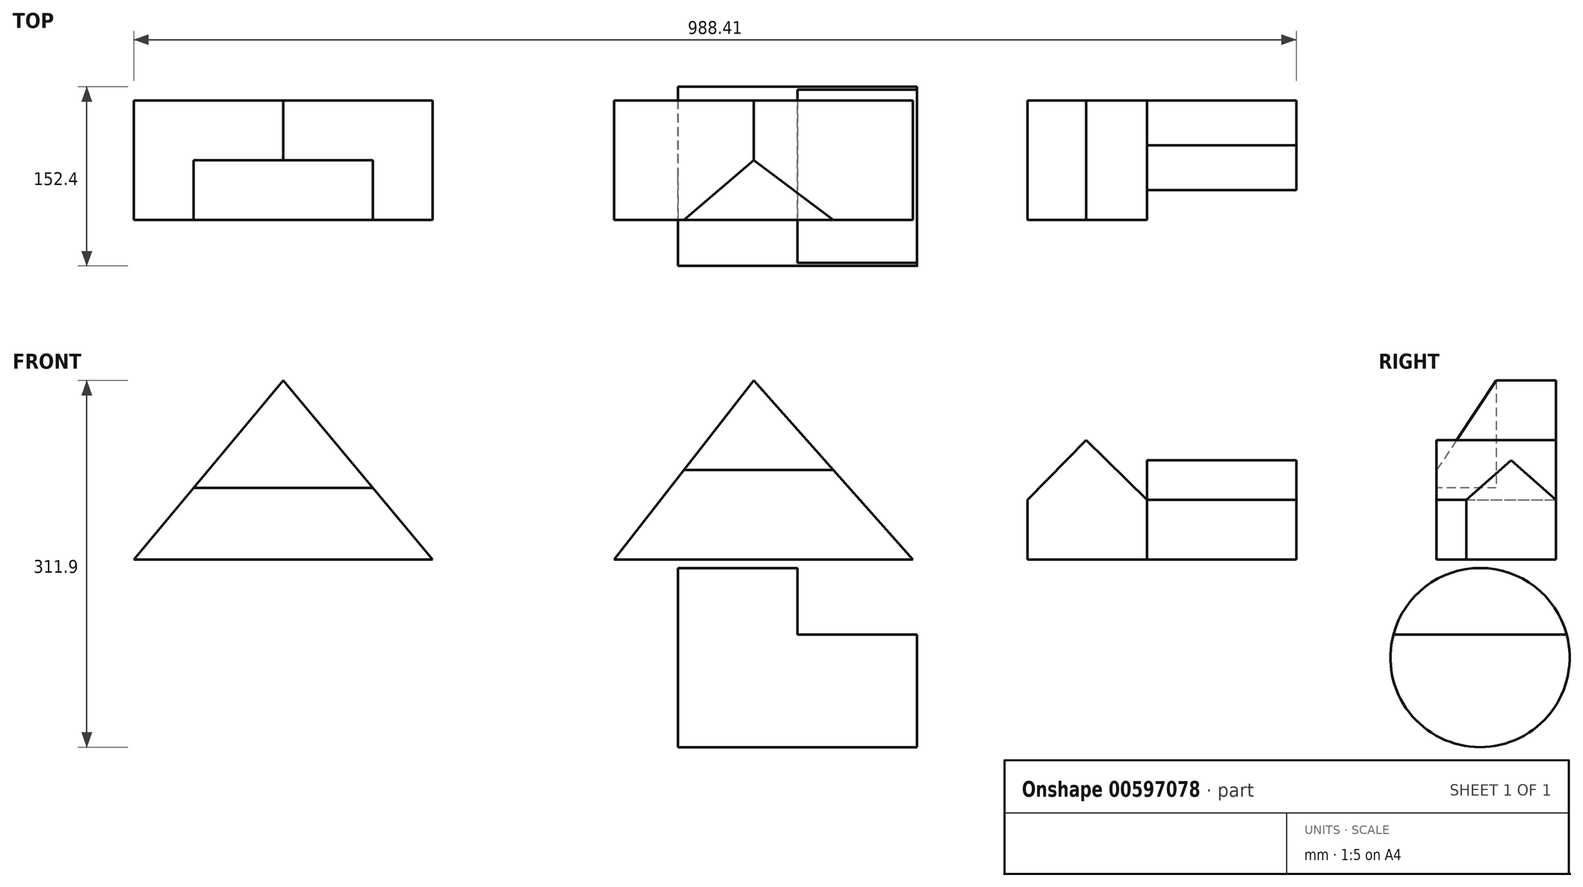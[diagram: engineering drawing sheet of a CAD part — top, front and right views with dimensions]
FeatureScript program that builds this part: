
annotation { "Feature Type Name" : "Feature", "Feature Type Description" : "" }
export const myFeature = defineFeature(function(context is Context, id is Id, definition is map)
    precondition{}
    {
        {
            var Q0;
            Q0=qCreatedBy(makeId("Front.planeOp"),FACE);
            var sketch = newSketch(context, id + "F0", { "sketchPlane" : qUnion([Q0])});
            skLineSegment(sketch, "E0", {"start": v(-127, 0) * mm, "end": v(127, 0) * mm});
            skLineSegment(sketch, "E1", {"start": v(127, 0) * mm, "end": v(0, 152.4) * mm});
            skLineSegment(sketch, "E2", {"start": v(0, 152.4) * mm, "end": v(-127, 0) * mm});
            skSolve(sketch);
        }
        {
            var Q0;
            Q0 = qSketchRegion(id + "F0", true);
            extrude(context, id + "F1", {"entities" : qUnion([Q0]), "depth" : 101.6 * mm, "offsetDistance" : 25.4 * mm});
        }
        {
            var Q0;
            Q0=makeQuery(id+"F1.opExtrude","CAP_FACE",FACE,{"disambiguationData":[OSD([sQuery(id+"F0.wireOp",EDGE,"E0"),sQuery(id+"F0.wireOp",EDGE,"E1"),sQuery(id+"F0.wireOp",EDGE,"E2")])],"isStart":false});
            var sketch = newSketch(context, id + "F2", { "sketchPlane" : qUnion([Q0])});
            skLineSegment(sketch, "E3", {"start": v(-76.2, 60.96) * mm, "end": v(76.2, 60.96) * mm});
            skLineSegment(sketch, "E4", {"start": v(76.2, 60.96) * mm, "end": v(0, 152.4) * mm});
            skLineSegment(sketch, "E5", {"start": v(0, 152.4) * mm, "end": v(-76.2, 60.96) * mm});
            skSolve(sketch);
        }
        {
            var Q0;
            Q0 = qSketchRegion(id + "F2", true);
            extrude(context, id + "F3", {"entities" : qUnion([Q0]), "operationType" : NewBodyOperationType.REMOVE, "oppositeDirection" : true, "depth" : 50.8 * mm, "offsetDistance" : 25.4 * mm});
        }
        {
            var Q0;
            Q0=qCreatedBy(makeId("Front.planeOp"),FACE);
            var sketch = newSketch(context, id + "F4", { "sketchPlane" : qUnion([Q0])});
            skLineSegment(sketch, "E6", {"start": v(281.3, 0) * mm, "end": v(535.3, 0) * mm});
            skLineSegment(sketch, "E7", {"start": v(535.3, 0) * mm, "end": v(400.1, 152.4) * mm});
            skLineSegment(sketch, "E8", {"start": v(400.1, 152.4) * mm, "end": v(281.3, 0) * mm});
            skSolve(sketch);
        }
        {
            var Q0;
            Q0 = qSketchRegion(id + "F4", true);
            extrude(context, id + "F5", {"entities" : qUnion([Q0]), "depth" : 101.6 * mm, "offsetDistance" : 25.4 * mm});
        }
        {
            var Q0;
            Q0=qCreatedBy(makeId("Right.planeOp"),FACE);
            cPlane(context, id + "F6", {"entities" : qUnion([Q0]), "cplaneType" : CPlaneType.OFFSET, "offset" : 539 * mm, "width" : 152.4 * mm, "height" : 152.4 * mm});
        }
        {
            var Q0;
            Q0=qCreatedBy(id+"F6.planeOp",FACE);
            var sketch = newSketch(context, id + "F7", { "sketchPlane" : qUnion([Q0])});
            skLineSegment(sketch, "E9", {"start": v(-101.6, 76.2) * mm, "end": v(-50.8, 152.4) * mm});
            skLineSegment(sketch, "E10", {"start": v(-50.8, 152.4) * mm, "end": v(-101.6, 152.4) * mm});
            skLineSegment(sketch, "E11", {"start": v(-101.6, 152.4) * mm, "end": v(-101.6, 76.2) * mm});
            skSolve(sketch);
        }
        {
            var Q0;
            Q0 = qSketchRegion(id + "F7", true);
            extrude(context, id + "F8", {"entities" : qUnion([Q0]), "operationType" : NewBodyOperationType.REMOVE, "oppositeDirection" : true, "depth" : 241.3 * mm, "offsetDistance" : 25.4 * mm});
        }
        {
            var Q0;
            Q0=qCreatedBy(makeId("Front.planeOp"),FACE);
            var sketch = newSketch(context, id + "F9", { "sketchPlane" : qUnion([Q0])});
            skLineSegment(sketch, "E12", {"start": v(632.81, 50.8) * mm, "end": v(632.81, 0) * mm});
            skLineSegment(sketch, "E13", {"start": v(632.81, 0) * mm, "end": v(734.41, 0) * mm});
            skLineSegment(sketch, "E14", {"start": v(734.41, 0) * mm, "end": v(734.41, 50.8) * mm});
            skLineSegment(sketch, "E15", {"start": v(734.41, 50.8) * mm, "end": v(682.72, 101.6) * mm});
            skLineSegment(sketch, "E16", {"start": v(682.72, 101.6) * mm, "end": v(632.81, 50.8) * mm});
            skSolve(sketch);
        }
        {
            var Q0;
            Q0 = qSketchRegion(id + "F9", true);
            extrude(context, id + "F10", {"entities" : qUnion([Q0]), "depth" : 101.6 * mm, "offsetDistance" : 25.4 * mm});
        }
        {
            var Q0;
            Q0=makeQuery(id+"F10.opExtrude","SWEPT_FACE",FACE,{"disambiguationData":[OSD([sQuery(id+"F9.wireOp",EDGE,"E14")])]});
            var sketch = newSketch(context, id + "F11", { "sketchPlane" : qUnion([Q0])});
            skLineSegment(sketch, "E17", {"start": v(0, 0) * mm, "end": v(-76.2, 0) * mm});
            skLineSegment(sketch, "E18", {"start": v(-76.2, 0) * mm, "end": v(-76.2, 50.8) * mm});
            skLineSegment(sketch, "E19", {"start": v(-76.2, 50.8) * mm, "end": v(-38.1, 84.4) * mm});
            skLineSegment(sketch, "E20", {"start": v(-38.1, 84.4) * mm, "end": v(0, 50.8) * mm});
            skLineSegment(sketch, "E21", {"start": v(0, 50.8) * mm, "end": v(0, 0) * mm});
            skSolve(sketch);
        }
        {
            var Q0;
            Q0 = qSketchRegion(id + "F11", true);
            extrude(context, id + "F12", {"entities" : qUnion([Q0]), "operationType" : NewBodyOperationType.ADD, "depth" : 127 * mm, "offsetDistance" : 25.4 * mm});
        }
        {
            var Q0;
            Q0=qCreatedBy(id+"F6.planeOp",FACE);
            var sketch = newSketch(context, id + "F13", { "sketchPlane" : qUnion([Q0])});
            skCircle(sketch, "E22", {"center": v(-64.66, -83.3) * mm, "radius": 76.2 * mm});
            skSolve(sketch);
        }
        {
            var Q0;
            Q0 = qSketchRegion(id + "F13", true);
            extrude(context, id + "F14", {"entities" : qUnion([Q0]), "oppositeDirection" : true, "depth" : 203.2 * mm, "offsetDistance" : 25.4 * mm});
        }
        {
            var Q0;
            Q0=makeQuery(id+"F14.opExtrude","CAP_FACE",FACE,{"disambiguationData":[OSD([sQuery(id+"F13.wireOp",EDGE,"E22")])],"isStart":true});
            var sketch = newSketch(context, id + "F15", { "sketchPlane" : qUnion([Q0])});
            skLineSegment(sketch, "E23", {"start": v(-138.3, -63.69) * mm, "end": v(8.98, -63.69) * mm});
            skSolve(sketch);
        }
        {
            var Q0;
            {var subQ0=sQuery(id+"F15.wireOp",EDGE,"E23");Q0=makeQuery(id+"F15.imprint","IMPRINT",FACE,{"disambiguationData":[TD([[makeQuery(id+"F15.imprint","IMPRINT",EDGE,{"derivedFrom":subQ0}),1.0]])]});}
            extrude(context, id + "F16", {"entities" : qUnion([Q0]), "operationType" : NewBodyOperationType.REMOVE, "oppositeDirection" : true, "depth" : 101.6 * mm, "offsetDistance" : 25.4 * mm});
        }
    });
